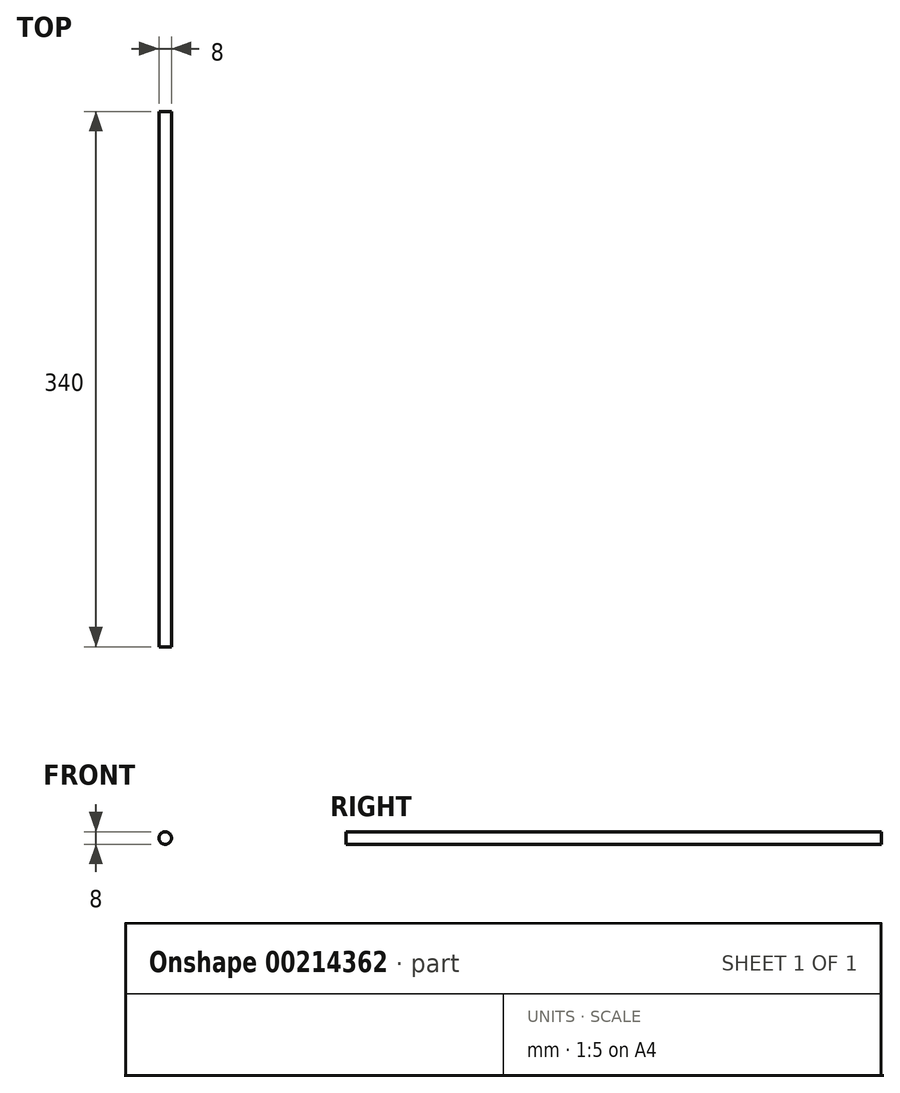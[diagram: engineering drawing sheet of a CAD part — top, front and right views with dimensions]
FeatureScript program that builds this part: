
annotation { "Feature Type Name" : "Feature", "Feature Type Description" : "" }
export const myFeature = defineFeature(function(context is Context, id is Id, definition is map)
    precondition{}
    {
        {
            var Q0;
            Q0=qCreatedBy(makeId("Front.planeOp"),FACE);
            var sketch = newSketch(context, id + "F0", { "sketchPlane" : qUnion([Q0])});
            skCircle(sketch, "E0", {"center": v(0, 0) * mm, "radius": 4 * mm});
            skSolve(sketch);
        }
        {
            var Q0;
            Q0=makeQuery(id+"F0.imprint","IMPRINT",FACE,{"disambiguationData":[TD([[makeQuery(id+"F0.imprint","IMPRINT",EDGE,{"derivedFrom":sQuery(id+"F0.wireOp",EDGE,"E0")}),1.0]])]});
            extrude(context, id + "F1", {"entities" : qUnion([Q0]), "depth" : 170 * mm, "hasSecondDirection" : true, "secondDirectionOppositeDirection" : true, "secondDirectionDepth" : 170 * mm});
        }
    });
